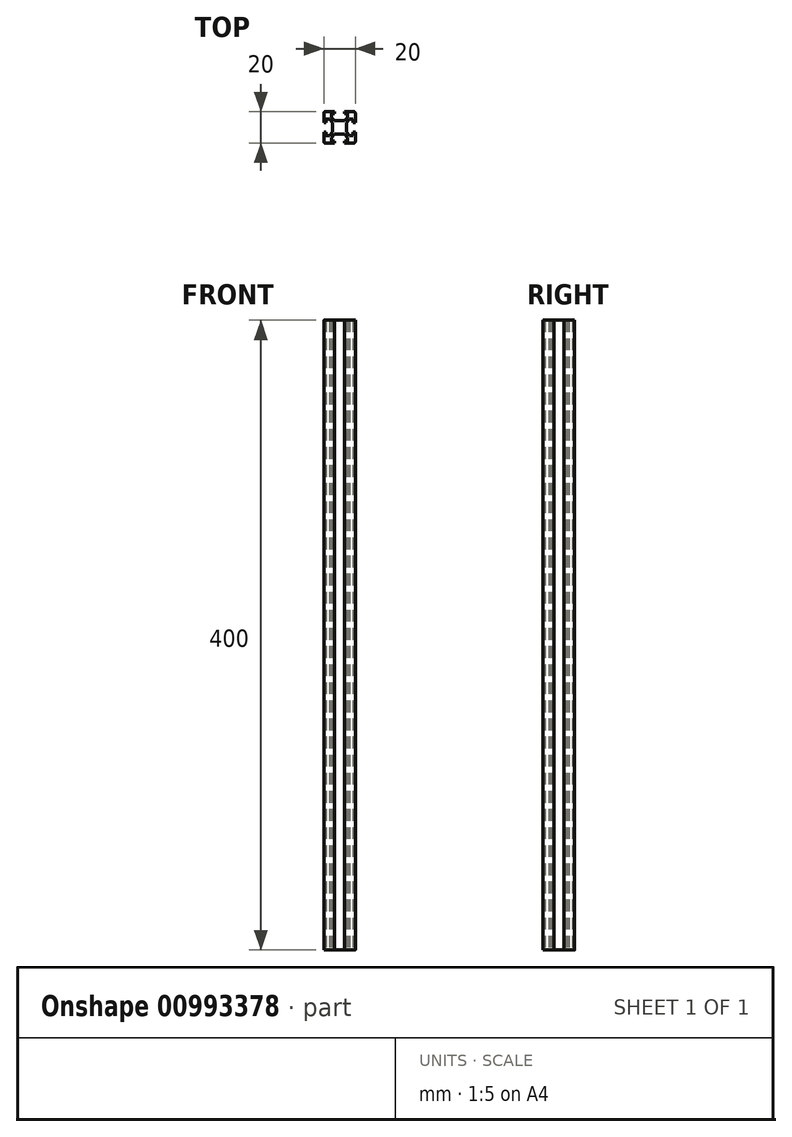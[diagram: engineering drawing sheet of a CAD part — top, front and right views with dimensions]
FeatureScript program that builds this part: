
annotation { "Feature Type Name" : "Feature", "Feature Type Description" : "" }
export const myFeature = defineFeature(function(context is Context, id is Id, definition is map)
    precondition{}
    {
        {
            var Q0;
            Q0=qCreatedBy(makeId("Top.planeOp"),FACE);
            var sketch = newSketch(context, id + "F0", { "sketchPlane" : qUnion([Q0])});
            skLineSegment(sketch, "E0.1", {"start": v(5.65, 6.9) * mm, "end": v(5.65, 13.1) * mm});
            skLineSegment(sketch, "E0.2", {"start": v(6.9, 5.65) * mm, "end": v(13.1, 5.65) * mm});
            skLineSegment(sketch, "E0.3", {"start": v(14.35, 6.9) * mm, "end": v(14.35, 13.1) * mm});
            skLineSegment(sketch, "E1", {"start": v(1, 20) * mm, "end": v(6.9, 20) * mm});
            skLineSegment(sketch, "E2", {"start": v(6.9, 20) * mm, "end": v(6.9, 18.7) * mm});
            skLineSegment(sketch, "E3", {"start": v(6.9, 18.7) * mm, "end": v(4.9, 18.7) * mm});
            skLineSegment(sketch, "E4", {"start": v(6.9, 14.35) * mm, "end": v(4.9, 16.35) * mm});
            skLineSegment(sketch, "E5", {"start": v(4.9, 18.7) * mm, "end": v(4.9, 16.35) * mm});
            skLineSegment(sketch, "E6.MirrorCS", {"start": v(0, 13.1) * mm, "end": v(1.3, 13.1) * mm});
            skLineSegment(sketch, "E7.MirrorCS", {"start": v(1.3, 13.1) * mm, "end": v(1.3, 15.1) * mm});
            skLineSegment(sketch, "E8.MirrorCS", {"start": v(1.3, 15.1) * mm, "end": v(3.65, 15.1) * mm});
            skLineSegment(sketch, "E9.MirrorCS", {"start": v(5.65, 13.1) * mm, "end": v(3.65, 15.1) * mm});
            skLineSegment(sketch, "E10", {"start": v(0, 19) * mm, "end": v(0, 13.1) * mm});
            skLineSegment(sketch, "E11.MirrorCS", {"start": v(13.1, 14.35) * mm, "end": v(15.1, 16.35) * mm});
            skLineSegment(sketch, "E12.MirrorCS", {"start": v(13.1, 18.7) * mm, "end": v(15.1, 18.7) * mm});
            skLineSegment(sketch, "E13.MirrorCS", {"start": v(13.1, 20) * mm, "end": v(13.1, 18.7) * mm});
            skLineSegment(sketch, "E14.MirrorCS", {"start": v(15.1, 18.7) * mm, "end": v(15.1, 16.35) * mm});
            skLineSegment(sketch, "E15.MirrorCS", {"start": v(14.35, 13.1) * mm, "end": v(16.35, 15.1) * mm});
            skLineSegment(sketch, "E16.MirrorCS", {"start": v(18.7, 15.1) * mm, "end": v(16.35, 15.1) * mm});
            skLineSegment(sketch, "E17.MirrorCS", {"start": v(18.7, 13.1) * mm, "end": v(18.7, 15.1) * mm});
            skLineSegment(sketch, "E18.MirrorCS", {"start": v(20, 13.1) * mm, "end": v(18.7, 13.1) * mm});
            skLineSegment(sketch, "E19.MirrorCS", {"start": v(20, 19) * mm, "end": v(20, 13.1) * mm});
            skLineSegment(sketch, "E20.MirrorCS", {"start": v(19, 20) * mm, "end": v(13.1, 20) * mm});
            skLineSegment(sketch, "E21.MirrorCS", {"start": v(0, 6.9) * mm, "end": v(1.3, 6.9) * mm});
            skLineSegment(sketch, "E22.MirrorCS", {"start": v(4.9, 1.3) * mm, "end": v(4.9, 3.65) * mm});
            skLineSegment(sketch, "E23.MirrorCS", {"start": v(1.3, 4.9) * mm, "end": v(3.65, 4.9) * mm});
            skLineSegment(sketch, "E24.MirrorCS", {"start": v(1.3, 6.9) * mm, "end": v(1.3, 4.9) * mm});
            skLineSegment(sketch, "E25.MirrorCS", {"start": v(5.65, 6.9) * mm, "end": v(3.65, 4.9) * mm});
            skLineSegment(sketch, "E26.MirrorCS", {"start": v(6.9, 5.65) * mm, "end": v(4.9, 3.65) * mm});
            skLineSegment(sketch, "E27.MirrorCS", {"start": v(6.9, 0) * mm, "end": v(6.9, 1.3) * mm});
            skLineSegment(sketch, "E28.MirrorCS", {"start": v(6.9, 1.3) * mm, "end": v(4.9, 1.3) * mm});
            skLineSegment(sketch, "E29.MirrorCS", {"start": v(18.7, 4.9) * mm, "end": v(16.35, 4.9) * mm});
            skLineSegment(sketch, "E30.MirrorCS", {"start": v(20, 6.9) * mm, "end": v(18.7, 6.9) * mm});
            skLineSegment(sketch, "E31.MirrorCS", {"start": v(15.1, 1.3) * mm, "end": v(15.1, 3.65) * mm});
            skLineSegment(sketch, "E32.MirrorCS", {"start": v(13.1, 0) * mm, "end": v(13.1, 1.3) * mm});
            skLineSegment(sketch, "E33.MirrorCS", {"start": v(13.1, 1.3) * mm, "end": v(15.1, 1.3) * mm});
            skLineSegment(sketch, "E34.MirrorCS", {"start": v(18.7, 6.9) * mm, "end": v(18.7, 4.9) * mm});
            skLineSegment(sketch, "E35.MirrorCS", {"start": v(19, 0) * mm, "end": v(13.1, 0) * mm});
            skLineSegment(sketch, "E36.MirrorCS", {"start": v(13.1, 5.65) * mm, "end": v(15.1, 3.65) * mm});
            skLineSegment(sketch, "E37.MirrorCS", {"start": v(20, 1) * mm, "end": v(20, 6.9) * mm});
            skLineSegment(sketch, "E38.MirrorCS", {"start": v(14.35, 6.9) * mm, "end": v(16.35, 4.9) * mm});
            skLineSegment(sketch, "E39", {"start": v(6.9, 14.35) * mm, "end": v(13.1, 14.35) * mm});
            skLineSegment(sketch, "E40", {"start": v(0, 6.9) * mm, "end": v(0, 1) * mm});
            skLineSegment(sketch, "E41", {"start": v(1, 0) * mm, "end": v(6.9, 0) * mm});
            skPoint(sketch, "E42.visualSharp", {"position": v(0, 20) * mm});
            skArc(sketch, "E42.filletArc", {"start": v(1, 20) * mm, "mid": v(0.3, 19.7) * mm, "end": v(0, 19) * mm});
            skPoint(sketch, "E43.visualSharp", {"position": v(20, 20) * mm});
            skArc(sketch, "E43.filletArc", {"start": v(20, 19) * mm, "mid": v(19.7, 19.7) * mm, "end": v(19, 20) * mm});
            skPoint(sketch, "E44.visualSharp", {"position": v(20, 0) * mm});
            skArc(sketch, "E44.filletArc", {"start": v(19, 0) * mm, "mid": v(19.7, 0.3) * mm, "end": v(20, 1) * mm});
            skPoint(sketch, "E45.visualSharp", {"position": v(0, 0) * mm});
            skArc(sketch, "E45.filletArc", {"start": v(0, 1) * mm, "mid": v(0.3, 0.3) * mm, "end": v(1, 0) * mm});
            skSolve(sketch);
        }
        {
            var Q0;
            Q0 = qSketchRegion(id + "F0", true);
            extrude(context, id + "F1", {"entities" : qUnion([Q0]), "depth" : 400 * mm, "offsetDistance" : 25 * mm});
        }
    });
